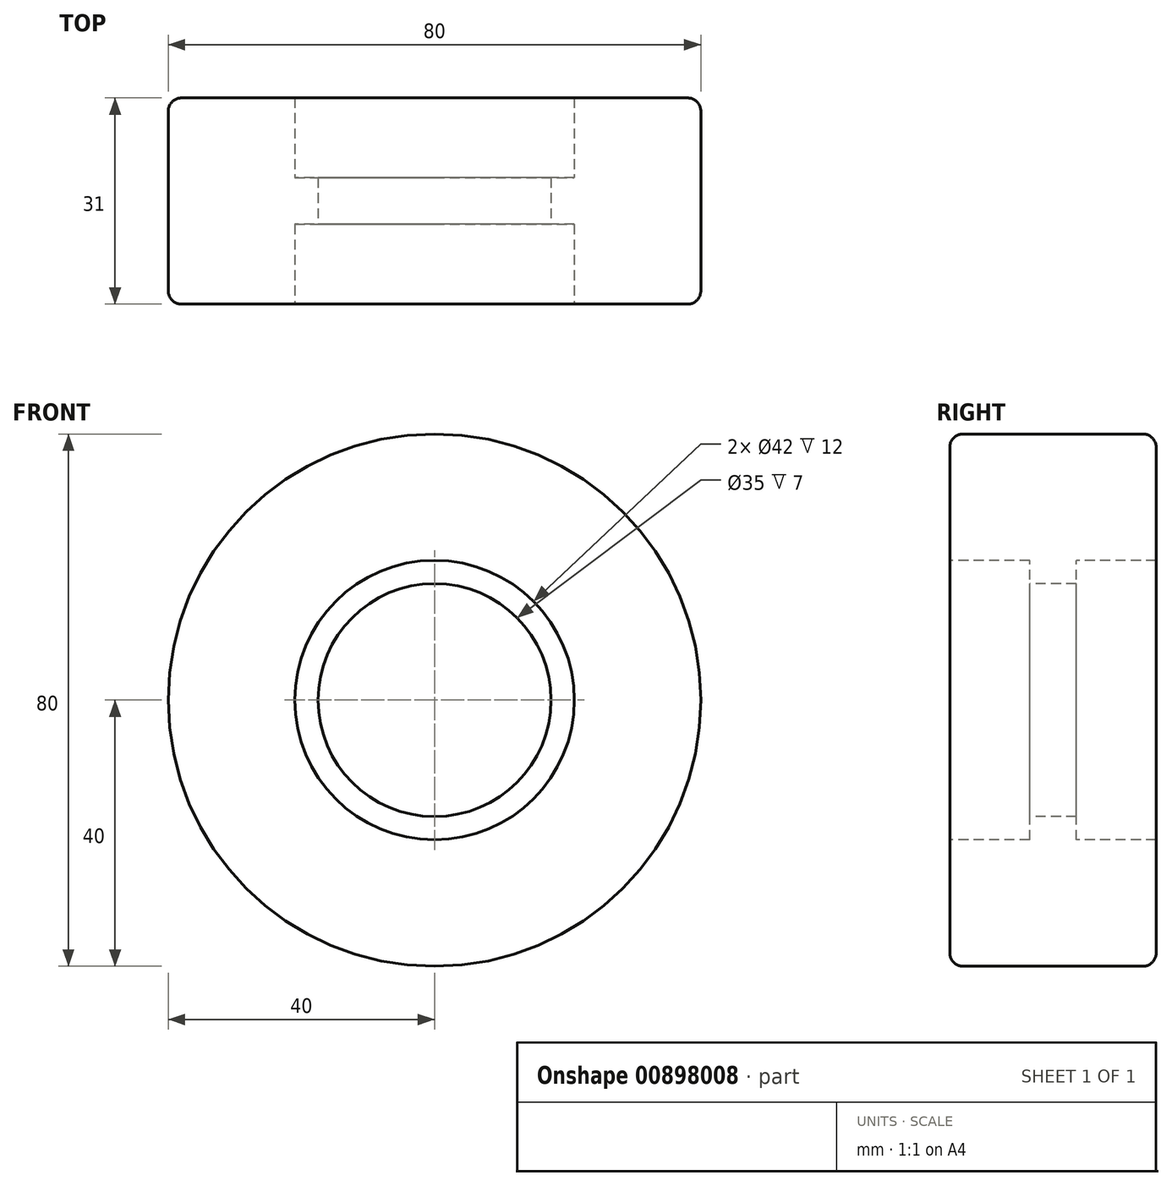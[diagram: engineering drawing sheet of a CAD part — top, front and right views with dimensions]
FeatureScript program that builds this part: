
annotation { "Feature Type Name" : "Feature", "Feature Type Description" : "" }
export const myFeature = defineFeature(function(context is Context, id is Id, definition is map)
    precondition{}
    {
        {
            var Q0;
            Q0=qCreatedBy(makeId("Right.planeOp"),FACE);
            var sketch = newSketch(context, id + "F0", { "sketchPlane" : qUnion([Q0])});
            skLineSegment(sketch, "E0", {"start": v(-34.65, 0) * mm, "end": v(45.53, 0) * mm, "construction": true});
            skLineSegment(sketch, "E1", {"start": v(-15.5, 21) * mm, "end": v(-15.5, 38) * mm});
            skLineSegment(sketch, "E2", {"start": v(-13.5, 40) * mm, "end": v(13.5, 40) * mm});
            skLineSegment(sketch, "E3", {"start": v(15.5, 38) * mm, "end": v(15.5, 21) * mm});
            skLineSegment(sketch, "E4", {"start": v(-15.5, 21) * mm, "end": v(-3.5, 21) * mm});
            skLineSegment(sketch, "E5", {"start": v(-3.5, 21) * mm, "end": v(-3.5, 17.5) * mm});
            skLineSegment(sketch, "E6", {"start": v(-3.5, 17.5) * mm, "end": v(3.5, 17.5) * mm});
            skLineSegment(sketch, "E7", {"start": v(3.5, 17.5) * mm, "end": v(3.5, 21) * mm});
            skLineSegment(sketch, "E8", {"start": v(3.5, 21) * mm, "end": v(15.5, 21) * mm});
            skPoint(sketch, "E9.visualSharp", {"position": v(-15.5, 40) * mm});
            skArc(sketch, "E9.filletArc", {"start": v(-13.5, 40) * mm, "mid": v(-14.91, 39.41) * mm, "end": v(-15.5, 38) * mm});
            skPoint(sketch, "E10.visualSharp", {"position": v(15.5, 40) * mm});
            skArc(sketch, "E10.filletArc", {"start": v(15.5, 38) * mm, "mid": v(14.91, 39.41) * mm, "end": v(13.5, 40) * mm});
            skSolve(sketch);
        }
        {
            var Q0;
            Q0 = qSketchRegion(id + "F0", true);
            var Q1;
            Q1=sQuery(id+"F0.wireOp",EDGE,"E0");
            revolve(context, id + "F1", {"surfaceOperationType" : NewSurfaceOperationType.NEW, "entities" : qUnion([Q0]), "axis" : qUnion([Q1]), "revolveType" : RevolveType.FULL});
        }
    });
